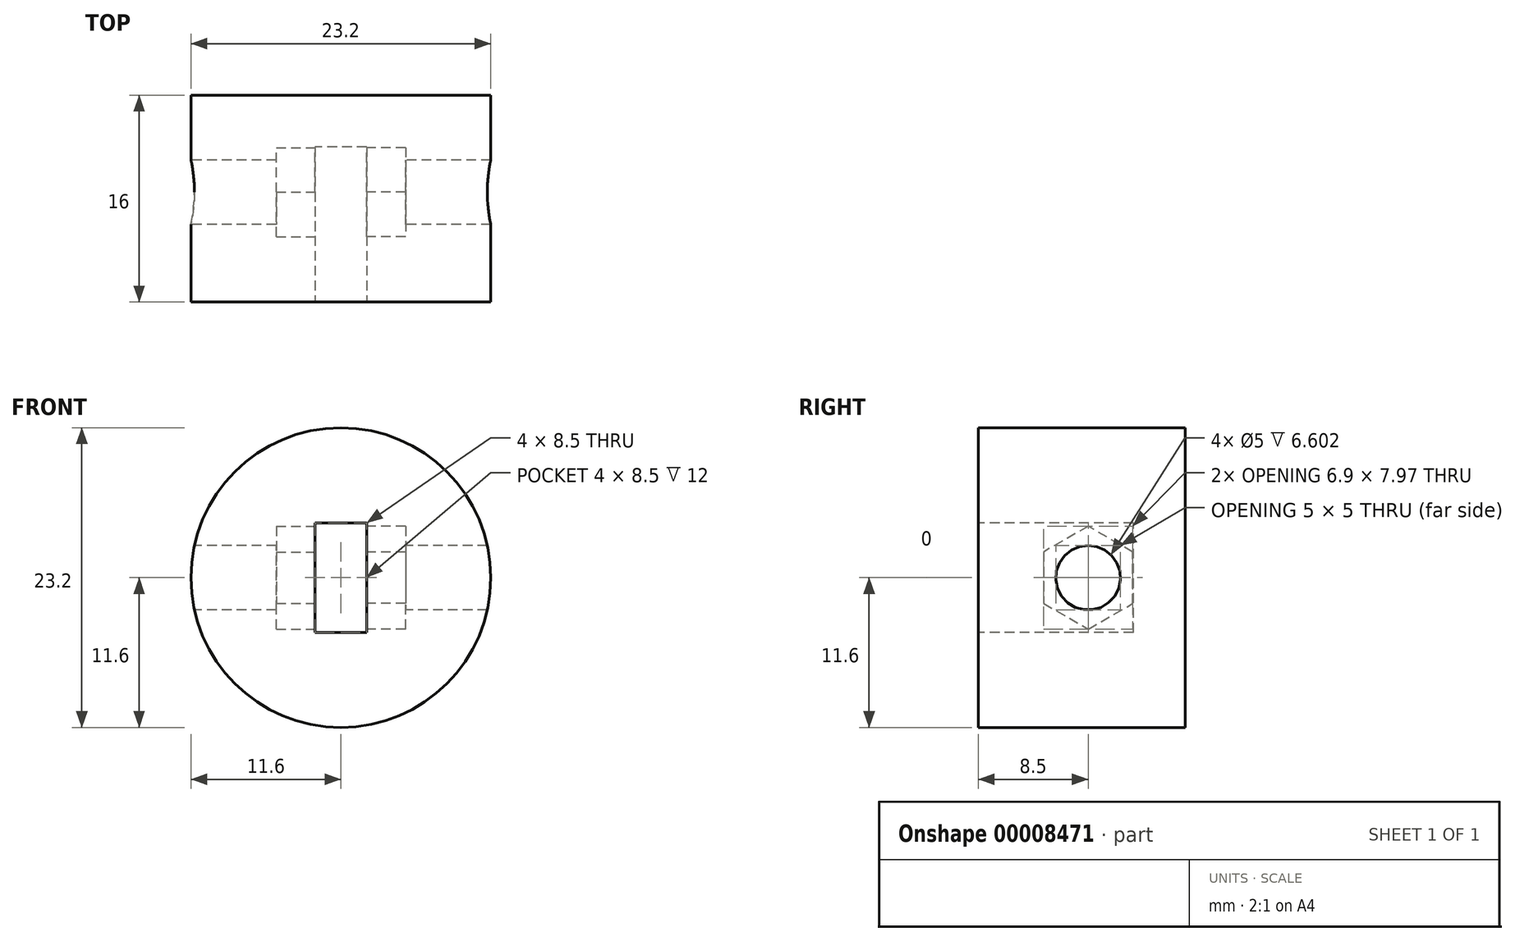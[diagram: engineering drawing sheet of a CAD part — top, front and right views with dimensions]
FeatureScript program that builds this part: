
annotation { "Feature Type Name" : "Feature", "Feature Type Description" : "" }
export const myFeature = defineFeature(function(context is Context, id is Id, definition is map)
    precondition{}
    {
        {
            var Q0;
            Q0=qCreatedBy(makeId("Front.planeOp"),FACE);
            var sketch = newSketch(context, id + "F0", { "sketchPlane" : qUnion([Q0])});
            skCircle(sketch, "E0", {"center": v(0, 0) * mm, "radius": 11.6 * mm});
            skSolve(sketch);
        }
        {
            var Q0;
            Q0 = qSketchRegion(id + "F0", true);
            extrude(context, id + "F1", {"entities" : qUnion([Q0]), "depth" : 16 * mm});
        }
        {
            var Q0;
            Q0=makeQuery(id+"F1.opExtrude","CAP_FACE",FACE,{"disambiguationData":[OSD([sQuery(id+"F0.wireOp",EDGE,"E0")])],"isStart":false});
            var sketch = newSketch(context, id + "F2", { "sketchPlane" : qUnion([Q0])});
            skLineSegment(sketch, "E1", {"start": v(-11.6, 0) * mm, "end": v(-11.6, 5.33) * mm});
            skSolve(sketch);
        }
        {
            var Q0;
            Q0 = qSketchRegion(id + "F2", true);
            var Q1;
            Q1=sQuery(id+"F2.wireOp",EDGE,"E1");
            extrude(context, id + "F3", {"entities" : qUnion([Q0]), "bodyType" : ToolBodyType.SURFACE, "surfaceEntities" : qUnion([Q1]), "oppositeDirection" : true, "depth" : 13.53 * mm});
        }
        {
            var Q0;
            Q0=makeQuery(id+"F3.opExtrude","SWEPT_FACE",FACE,{"disambiguationData":[OSD([sQuery(id+"F2.wireOp",EDGE,"E1")])]});
            var sketch = newSketch(context, id + "F4", { "sketchPlane" : qUnion([Q0])});
            skCircle(sketch, "E2", {"center": v(7.5, 0) * mm, "radius": 2.5 * mm});
            skSolve(sketch);
        }
        {
            var Q0;
            {var subQ0=sQuery(id+"F4.wireOp",EDGE,"E2");var subQ1=makeQuery(id+"F3.opExtrude","SWEPT_EDGE",EDGE,{"disambiguationData":[OSD([sQuery(id+"F2.wireOp",VERTEX,"E1.start")])]});var subQ2=makeQuery(id+"F4.imprint","INTERSECT",VERTEX,{"disambiguationData":[OD(0.0)],"derivedFrom":[subQ1,subQ0]});Q0=makeQuery(id+"F4.imprint","IMPRINT",FACE,{"disambiguationData":[TD([[makeQuery(id+"F4.imprint","IMPRINT",EDGE,{"disambiguationData":[TD([[subQ2,1.0]])],"derivedFrom":subQ0}),1.0]])]});}
            var Q1;
            {var subQ0=sQuery(id+"F4.wireOp",EDGE,"E2");var subQ1=makeQuery(id+"F3.opExtrude","SWEPT_EDGE",EDGE,{"disambiguationData":[OSD([sQuery(id+"F2.wireOp",VERTEX,"E1.start")])]});var subQ2=makeQuery(id+"F4.imprint","INTERSECT",VERTEX,{"disambiguationData":[OD(0.0)],"derivedFrom":[subQ1,subQ0]});Q1=makeQuery(id+"F4.imprint","IMPRINT",FACE,{"disambiguationData":[TD([[makeQuery(id+"F4.imprint","IMPRINT",EDGE,{"disambiguationData":[TD([[subQ2,-1.0]])],"derivedFrom":subQ0}),1.0]])]});}
            extrude(context, id + "F5", {"entities" : qUnion([Q0, Q1]), "operationType" : NewBodyOperationType.REMOVE, "endBound" : BoundingType.THROUGH_ALL, "oppositeDirection" : true, "depth" : 25 * mm});
        }
        {
            var Q0;
            Q0=makeQuery(id+"F1.opExtrude","CAP_FACE",FACE,{"disambiguationData":[OSD([sQuery(id+"F0.wireOp",EDGE,"E0")])],"isStart":false});
            var sketch = newSketch(context, id + "F6", { "sketchPlane" : qUnion([Q0])});
            skLineSegment(sketch, "E3.bottom", {"start": v(2, -4.25) * mm, "end": v(-2, -4.25) * mm});
            skLineSegment(sketch, "E3.top", {"start": v(2, 4.25) * mm, "end": v(-2, 4.25) * mm});
            skLineSegment(sketch, "E3.left", {"start": v(2, -4.25) * mm, "end": v(2, 4.25) * mm});
            skLineSegment(sketch, "E3.right", {"start": v(-2, -4.25) * mm, "end": v(-2, 4.25) * mm});
            skPoint(sketch, "E3.middle", {"position": v(0, 0) * mm});
            skSolve(sketch);
        }
        {
            var Q0;
            Q0 = qSketchRegion(id + "F6", true);
            extrude(context, id + "F7", {"entities" : qUnion([Q0]), "operationType" : NewBodyOperationType.REMOVE, "oppositeDirection" : true, "depth" : 12 * mm});
        }
        {
            var Q0;
            Q0=makeQuery(id+"F7.boolean.opBoolean","COPY",FACE,{"derivedFrom":makeQuery(id+"F7.opExtrude","SWEPT_FACE",FACE,{"disambiguationData":[OSD([sQuery(id+"F6.wireOp",EDGE,"E3.right")])]})});
            var sketch = newSketch(context, id + "F8", { "sketchPlane" : qUnion([Q0])});
            skCircle(sketch, "E4.cCircle", {"center": v(-7.5, 0) * mm, "radius": 3.45 * mm, "construction": true});
            skLineSegment(sketch, "E4.0", {"start": v(-4.05, 2) * mm, "end": v(-4.05, -2) * mm});
            skLineSegment(sketch, "E4.1", {"start": v(-4.05, -2) * mm, "end": v(-7.5, -3.98) * mm});
            skLineSegment(sketch, "E4.2", {"start": v(-7.5, -3.98) * mm, "end": v(-10.95, -2) * mm});
            skLineSegment(sketch, "E4.3", {"start": v(-10.95, -2) * mm, "end": v(-10.95, 2) * mm});
            skLineSegment(sketch, "E4.4", {"start": v(-10.95, 2) * mm, "end": v(-7.5, 3.98) * mm});
            skLineSegment(sketch, "E4.5", {"start": v(-7.5, 3.98) * mm, "end": v(-4.05, 2) * mm});
            skPoint(sketch, "E4.0.midPoint", {"position": v(-4.05, 0) * mm});
            skSolve(sketch);
        }
        {
            var Q0;
            Q0=makeQuery(id+"F8.imprint","IMPRINT",FACE,{"disambiguationData":[TD([[makeQuery(id+"F8.imprint","IMPRINT",EDGE,{"derivedFrom":sQuery(id+"F8.wireOp",EDGE,"E4.0")}),-1.0]])]});
            extrude(context, id + "F9", {"entities" : qUnion([Q0]), "operationType" : NewBodyOperationType.REMOVE, "oppositeDirection" : true, "depth" : 3 * mm});
        }
        {
            var Q0;
            Q0=makeQuery(id+"F7.boolean.opBoolean","COPY",FACE,{"derivedFrom":makeQuery(id+"F7.opExtrude","SWEPT_FACE",FACE,{"disambiguationData":[OSD([sQuery(id+"F6.wireOp",EDGE,"E3.left")])]})});
            var sketch = newSketch(context, id + "F10", { "sketchPlane" : qUnion([Q0])});
            skCircle(sketch, "E5.cCircle", {"center": v(7.5, 0) * mm, "radius": 3.45 * mm, "construction": true});
            skPoint(sketch, "E5.cCircle.perimeterSnap0", {"position": v(16, 0) * mm});
            skLineSegment(sketch, "E5.0", {"start": v(10.95, 2) * mm, "end": v(10.95, -2) * mm});
            skLineSegment(sketch, "E5.1", {"start": v(10.95, -2) * mm, "end": v(7.5, -3.98) * mm});
            skLineSegment(sketch, "E5.2", {"start": v(7.5, -3.98) * mm, "end": v(4.05, -2) * mm});
            skLineSegment(sketch, "E5.3", {"start": v(4.05, -2) * mm, "end": v(4.05, 2) * mm});
            skLineSegment(sketch, "E5.4", {"start": v(4.05, 2) * mm, "end": v(7.5, 3.98) * mm});
            skLineSegment(sketch, "E5.5", {"start": v(7.5, 3.98) * mm, "end": v(10.95, 2) * mm});
            skPoint(sketch, "E5.0.midPoint", {"position": v(10.95, 0) * mm});
            skPoint(sketch, "E5.0.midPoint.positionSnap0", {"position": v(16, 0) * mm});
            skSolve(sketch);
        }
        {
            var Q0;
            Q0 = qSketchRegion(id + "F10", true);
            extrude(context, id + "F11", {"entities" : qUnion([Q0]), "operationType" : NewBodyOperationType.REMOVE, "oppositeDirection" : true, "depth" : 3 * mm});
        }
    });
